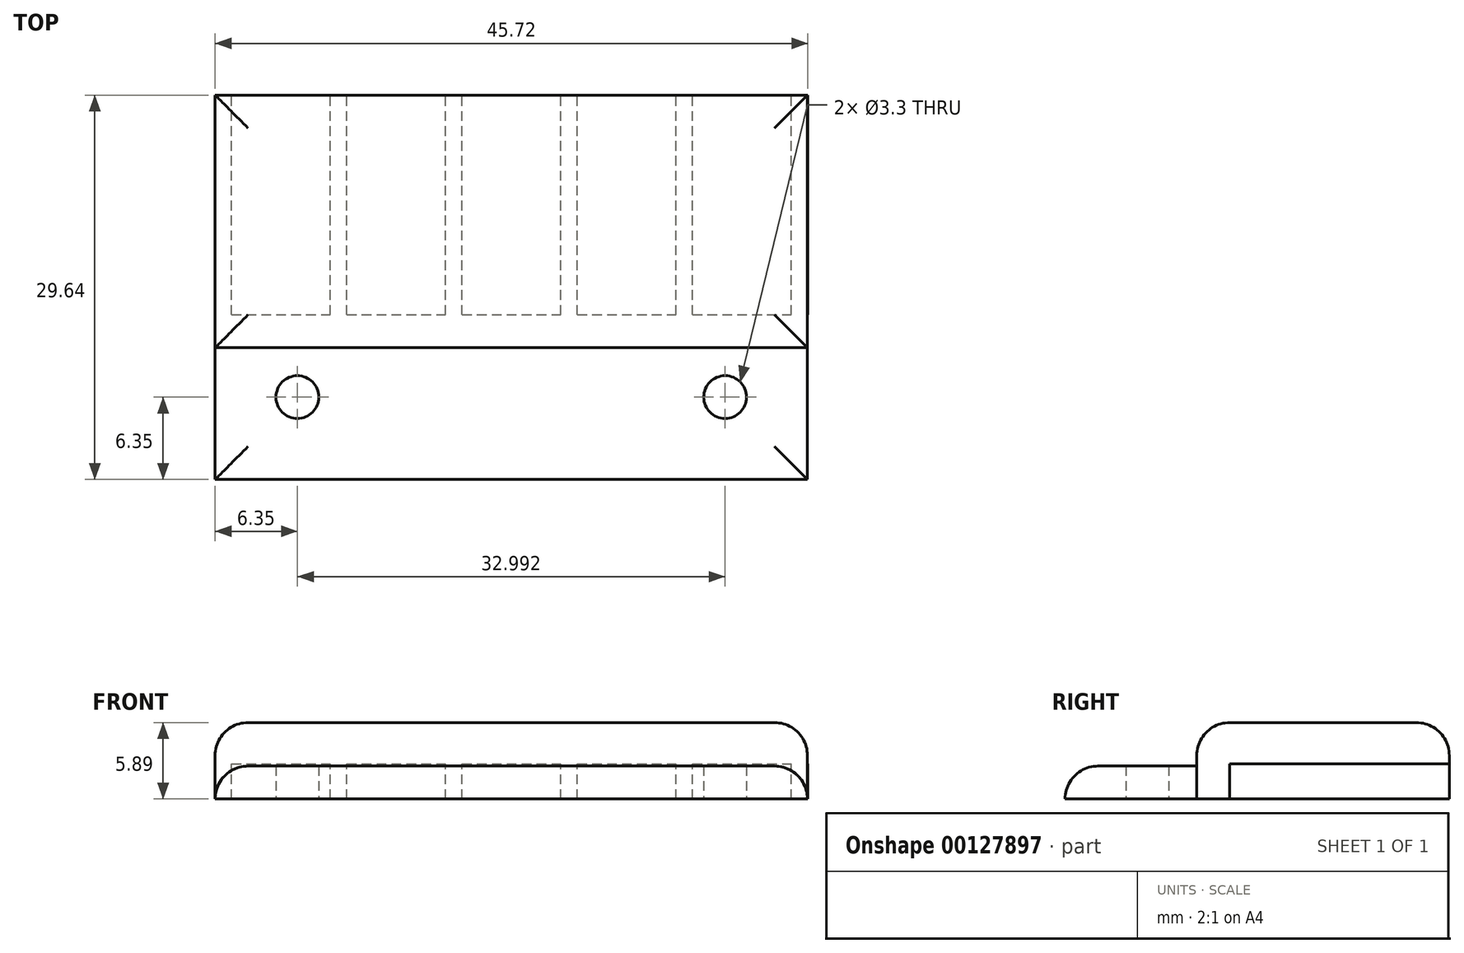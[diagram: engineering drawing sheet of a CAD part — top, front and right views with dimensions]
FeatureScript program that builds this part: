
annotation { "Feature Type Name" : "Feature", "Feature Type Description" : "" }
export const myFeature = defineFeature(function(context is Context, id is Id, definition is map)
    precondition{}
    {
        {
            var Q0;
            Q0=qCreatedBy(makeId("Top.planeOp"),FACE);
            var sketch = newSketch(context, id + "F0", { "sketchPlane" : qUnion([Q0])});
            skLineSegment(sketch, "E0.bottom", {"start": v(0, 0) * mm, "end": v(45.7, 0) * mm});
            skLineSegment(sketch, "E0.top", {"start": v(0, 12.7) * mm, "end": v(45.7, 12.7) * mm});
            skLineSegment(sketch, "E0.left", {"start": v(0, 0) * mm, "end": v(0, 12.7) * mm});
            skLineSegment(sketch, "E0.right", {"start": v(45.7, 0) * mm, "end": v(45.7, 12.7) * mm});
            skCircle(sketch, "E1", {"center": v(39.34, 6.35) * mm, "radius": 1.65 * mm});
            skCircle(sketch, "E2", {"center": v(6.35, 6.35) * mm, "radius": 1.65 * mm});
            skPoint(sketch, "E3.orphan", {"position": v(22.85, 0) * mm});
            skPoint(sketch, "E4.start.orphan", {"position": v(22.85, 12.7) * mm});
            skPoint(sketch, "E5.start.orphan", {"position": v(45.7, 6.35) * mm});
            skSolve(sketch);
        }
        {
            var Q0;
            Q0=makeQuery(id+"F0.imprint","IMPRINT",FACE,{"disambiguationData":[TD([[makeQuery(id+"F0.imprint","IMPRINT",EDGE,{"derivedFrom":sQuery(id+"F0.wireOp",EDGE,"E0.bottom")}),1.0]])]});
            extrude(context, id + "F1", {"entities" : qUnion([Q0]), "depth" : 2.54 * mm});
        }
        {
            var Q0;
            Q0=makeQuery(id+"F1.opExtrude","CAP_FACE",FACE,{"disambiguationData":[OSD([sQuery(id+"F0.wireOp",EDGE,"E0.bottom"),sQuery(id+"F0.wireOp",EDGE,"E0.top"),sQuery(id+"F0.wireOp",EDGE,"E0.left"),sQuery(id+"F0.wireOp",EDGE,"E0.right"),sQuery(id+"F0.wireOp",EDGE,"E1"),sQuery(id+"F0.wireOp",EDGE,"E2")])],"isStart":false});
            var sketch = newSketch(context, id + "F2", { "sketchPlane" : qUnion([Q0])});
            skLineSegment(sketch, "E6.bottom", {"start": v(0, 12.7) * mm, "end": v(45.7, 12.7) * mm});
            skLineSegment(sketch, "E6.top", {"start": v(0, 10.16) * mm, "end": v(45.7, 10.16) * mm});
            skLineSegment(sketch, "E6.left", {"start": v(0, 12.7) * mm, "end": v(0, 10.16) * mm});
            skLineSegment(sketch, "E6.right", {"start": v(45.7, 12.7) * mm, "end": v(45.7, 10.16) * mm});
            skSolve(sketch);
        }
        {
            var Q0;
            Q0 = qSketchRegion(id + "F2", true);
            extrude(context, id + "F3", {"entities" : qUnion([Q0]), "operationType" : NewBodyOperationType.ADD, "depth" : ((.119 + .16) - .1) * mm});
        }
        {
            var Q0;
            Q0=makeQuery(id+"F3.opExtrude","CAP_FACE",FACE,{"disambiguationData":[OSD([sQuery(id+"F2.wireOp",EDGE,"E6.bottom"),sQuery(id+"F2.wireOp",EDGE,"E6.top"),sQuery(id+"F2.wireOp",EDGE,"E6.left"),sQuery(id+"F2.wireOp",EDGE,"E6.right")])],"isStart":false});
            var sketch = newSketch(context, id + "F4", { "sketchPlane" : qUnion([Q0])});
            skLineSegment(sketch, "E7.bottom", {"start": v(0, 10.16) * mm, "end": v(45.7, 10.16) * mm});
            skLineSegment(sketch, "E7.top", {"start": v(0, 29.64) * mm, "end": v(45.7, 29.64) * mm});
            skLineSegment(sketch, "E7.left", {"start": v(0, 10.16) * mm, "end": v(0, 29.64) * mm});
            skLineSegment(sketch, "E7.right", {"start": v(45.7, 10.16) * mm, "end": v(45.7, 29.64) * mm});
            skSolve(sketch);
        }
        {
            var Q0;
            {var subQ0=sQuery(id+"F4.wireOp",EDGE,"E7.top");Q0=makeQuery(id+"F4.imprint","IMPRINT",FACE,{"disambiguationData":[TD([[makeQuery(id+"F4.imprint","IMPRINT",EDGE,{"derivedFrom":subQ0}),-1.0]])]});}
            var Q1;
            {var subQ0=sQuery(id+"F4.wireOp",EDGE,"E7.bottom");Q1=makeQuery(id+"F4.imprint","IMPRINT",FACE,{"disambiguationData":[TD([[makeQuery(id+"F4.imprint","IMPRINT",EDGE,{"derivedFrom":subQ0}),1.0]])]});}
            extrude(context, id + "F5", {"entities" : qUnion([Q0, Q1]), "operationType" : NewBodyOperationType.ADD, "depth" : 3.17 * mm});
        }
        {
            var Q0;
            Q0=makeQuery(id+"F5.opExtrude","CAP_EDGE",EDGE,{"disambiguationData":[OSD([sQuery(id+"F4.wireOp",EDGE,"E7.bottom")])],"isStart":false});
            var Q1;
            Q1=makeQuery(id+"F5.opExtrude","CAP_EDGE",EDGE,{"disambiguationData":[OSD([sQuery(id+"F4.wireOp",EDGE,"E7.top")])],"isStart":false});
            var Q2;
            Q2=makeQuery(id+"F5.opExtrude","CAP_EDGE",EDGE,{"disambiguationData":[OSD([sQuery(id+"F4.wireOp",EDGE,"E7.left")])],"isStart":false});
            var Q3;
            Q3=makeQuery(id+"F5.opExtrude","CAP_EDGE",EDGE,{"disambiguationData":[OSD([sQuery(id+"F4.wireOp",EDGE,"E7.right")])],"isStart":false});
            var Q4;
            Q4=makeQuery(id+"F1.opExtrude","CAP_EDGE",EDGE,{"disambiguationData":[OSD([sQuery(id+"F0.wireOp",EDGE,"E0.left")])],"isStart":false});
            var Q5;
            Q5=makeQuery(id+"F1.opExtrude","CAP_EDGE",EDGE,{"disambiguationData":[OSD([sQuery(id+"F0.wireOp",EDGE,"E0.bottom")])],"isStart":false});
            var Q6;
            Q6=makeQuery(id+"F1.opExtrude","CAP_EDGE",EDGE,{"disambiguationData":[OSD([sQuery(id+"F0.wireOp",EDGE,"E0.right")])],"isStart":false});
            var Q7;
            Q7=makeQuery(id+"F3.opExtrude","CAP_EDGE",EDGE,{"disambiguationData":[OSD([sQuery(id+"F2.wireOp",EDGE,"E6.top")])],"isStart":true});
            fillet(context, id + "F6", {"entities" : qUnion([Q0, Q1, Q2, Q3, Q4, Q5, Q6, Q7]), "radius" : 2.54 * mm, "tangentPropagation" : true, "allowEdgeOverflow" : false});
        }
        {
            var Q0;
            Q0=makeQuery(id+"F5.opExtrude","CAP_FACE",FACE,{"disambiguationData":[OSD([sQuery(id+"F4.wireOp",EDGE,"E7.bottom"),sQuery(id+"F4.wireOp",EDGE,"E7.top"),sQuery(id+"F4.wireOp",EDGE,"E7.left"),sQuery(id+"F4.wireOp",EDGE,"E7.right")])],"isStart":true});
            var sketch = newSketch(context, id + "F7", { "sketchPlane" : qUnion([Q0])});
            skLineSegment(sketch, "E8.bottom", {"start": v(0, -12.7) * mm, "end": v(1.27, -12.7) * mm});
            skLineSegment(sketch, "E8.top", {"start": v(0, -29.64) * mm, "end": v(1.27, -29.64) * mm});
            skLineSegment(sketch, "E8.left", {"start": v(0, -12.7) * mm, "end": v(0, -29.64) * mm});
            skLineSegment(sketch, "E8.right", {"start": v(1.27, -12.7) * mm, "end": v(1.27, -29.64) * mm});
            skLineSegment(sketch, "E9.1.0.0", {"start": v(10.16, -12.7) * mm, "end": v(10.16, -29.64) * mm});
            skLineSegment(sketch, "E9.1.0.1", {"start": v(8.89, -12.7) * mm, "end": v(10.16, -12.7) * mm});
            skLineSegment(sketch, "E9.1.0.2", {"start": v(8.89, -12.7) * mm, "end": v(8.89, -29.64) * mm});
            skLineSegment(sketch, "E9.1.0.3", {"start": v(8.89, -29.64) * mm, "end": v(10.16, -29.64) * mm});
            skLineSegment(sketch, "E9.2.0.0", {"start": v(19.05, -12.7) * mm, "end": v(19.05, -29.64) * mm});
            skLineSegment(sketch, "E9.2.0.1", {"start": v(17.78, -12.7) * mm, "end": v(19.05, -12.7) * mm});
            skLineSegment(sketch, "E9.2.0.2", {"start": v(17.78, -12.7) * mm, "end": v(17.78, -29.64) * mm});
            skLineSegment(sketch, "E9.2.0.3", {"start": v(17.78, -29.64) * mm, "end": v(19.05, -29.64) * mm});
            skLineSegment(sketch, "E9.3.0.0", {"start": v(27.94, -12.7) * mm, "end": v(27.94, -29.64) * mm});
            skLineSegment(sketch, "E9.3.0.1", {"start": v(26.67, -12.7) * mm, "end": v(27.94, -12.7) * mm});
            skLineSegment(sketch, "E9.3.0.2", {"start": v(26.67, -12.7) * mm, "end": v(26.67, -29.64) * mm});
            skLineSegment(sketch, "E9.3.0.3", {"start": v(26.67, -29.64) * mm, "end": v(27.94, -29.64) * mm});
            skLineSegment(sketch, "E9.4.0.0", {"start": v(36.83, -12.7) * mm, "end": v(36.83, -29.64) * mm});
            skLineSegment(sketch, "E9.4.0.1", {"start": v(35.56, -12.7) * mm, "end": v(36.83, -12.7) * mm});
            skLineSegment(sketch, "E9.4.0.2", {"start": v(35.56, -12.7) * mm, "end": v(35.56, -29.64) * mm});
            skLineSegment(sketch, "E9.4.0.3", {"start": v(35.56, -29.64) * mm, "end": v(36.83, -29.64) * mm});
            skLineSegment(sketch, "E9.5.0.0", {"start": v(45.72, -12.7) * mm, "end": v(45.72, -29.64) * mm});
            skLineSegment(sketch, "E9.5.0.1", {"start": v(44.45, -12.7) * mm, "end": v(45.72, -12.7) * mm});
            skLineSegment(sketch, "E9.5.0.2", {"start": v(44.45, -12.7) * mm, "end": v(44.45, -29.64) * mm});
            skLineSegment(sketch, "E9.5.0.3", {"start": v(44.45, -29.64) * mm, "end": v(45.72, -29.64) * mm});
            skLineSegment(sketch, "E9.direction1", {"start": v(1.27, -29.64) * mm, "end": v(10.16, -29.64) * mm, "construction": true});
            skSolve(sketch);
        }
        {
            var Q0;
            Q0 = qSketchRegion(id + "F7", true);
            var Q1;
            Q1=makeQuery(id+"F1.opExtrude","CAP_FACE",FACE,{"disambiguationData":[OSD([sQuery(id+"F0.wireOp",EDGE,"E0.bottom"),sQuery(id+"F0.wireOp",EDGE,"E0.top"),sQuery(id+"F0.wireOp",EDGE,"E0.left"),sQuery(id+"F0.wireOp",EDGE,"E0.right"),sQuery(id+"F0.wireOp",EDGE,"E1"),sQuery(id+"F0.wireOp",EDGE,"E2")])],"isStart":true});
            extrude(context, id + "F8", {"entities" : qUnion([Q0]), "operationType" : NewBodyOperationType.ADD, "endBound" : BoundingType.UP_TO_SURFACE, "endBoundEntityFace" : qUnion([Q1]), "depth" : 25.4 * mm});
        }
    });
